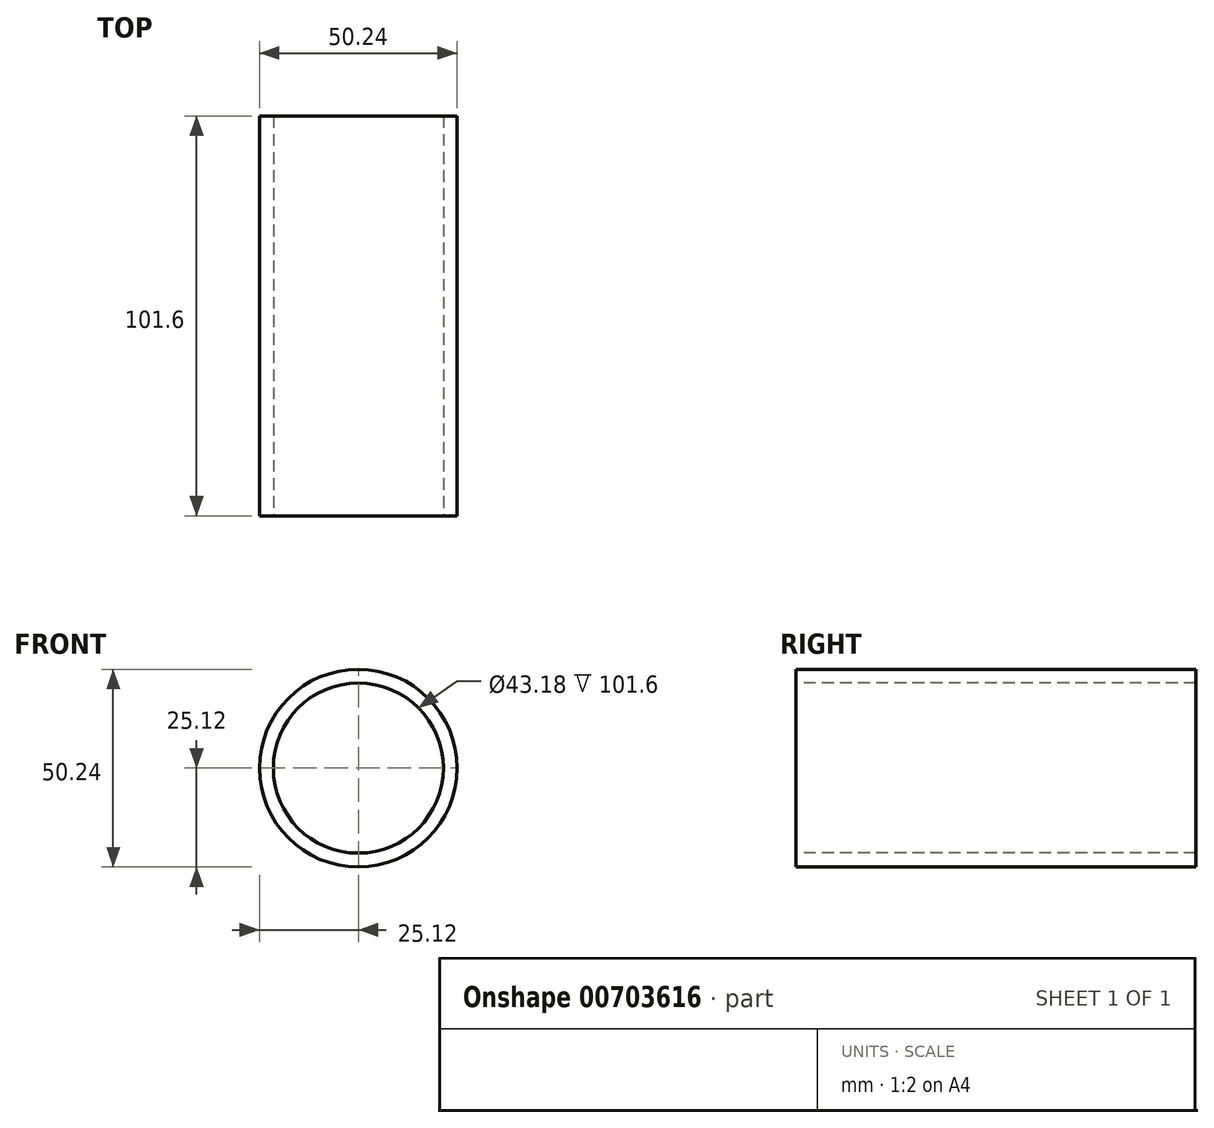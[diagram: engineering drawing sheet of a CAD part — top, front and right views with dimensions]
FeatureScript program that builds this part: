
annotation { "Feature Type Name" : "Feature", "Feature Type Description" : "" }
export const myFeature = defineFeature(function(context is Context, id is Id, definition is map)
    precondition{}
    {
        {
            var Q0;
            Q0=qCreatedBy(makeId("Front.planeOp"),FACE);
            var sketch = newSketch(context, id + "F0", { "sketchPlane" : qUnion([Q0])});
            skCircle(sketch, "E0", {"center": v(0, 0) * mm, "radius": 25.12 * mm});
            skCircle(sketch, "E1", {"center": v(0, 0) * mm, "radius": 21.59 * mm});
            skSolve(sketch);
        }
        {
            var Q0;
            Q0=makeQuery(id+"F0.imprint","IMPRINT",FACE,{"disambiguationData":[TD([[makeQuery(id+"F0.imprint","IMPRINT",EDGE,{"derivedFrom":sQuery(id+"F0.wireOp",EDGE,"E0")}),1.0]])]});
            extrude(context, id + "F1", {"entities" : qUnion([Q0]), "oppositeDirection" : true, "depth" : 101.6 * mm, "offsetDistance" : 25.4 * mm});
        }
    });
